# Revit family: 18-P-SD
name_source: partatom
category: Lighting Fixtures
revit_build: Autodesk Revit 2014 (Build: 20130308_1515(x64)
units: mm (PartAtom-declared; Revit-internal decimal feet)

## types (3) — shared parameters
Apparent Load = 0 VA
Assembly Code = D5020200
Circuiting = 1C 1 Circuit,2C 2 Circuit-In Board/ Out Board,AC Alternate Lamp Compart Switch
Color Filter = 16777215
Default Elevation = 4' - 0"
Description = The SDx is a semi-direct extruded aluminum fixture which can be pendant- or surface-mounted, using T8, T5, or T5HO lamps.
Diffuser = Blade Baffle, White/ Acrylic Blade Baffle, Green/ Parabolic Baffle, Semi-Specular Aluminum
Dimming Lamp Color Temperature Shift = <None>
Emit Shape Visible in Rendering = No
Emit from Rectangle Length = 0' - 4 1/2"
Finish/ Color = C1 CWM- Matte White,C2 TCWM- Textured Matte White,C3 CSL- Light Silver,C4 CMA- Machined Aluminum,C5 CCB- Carbon Black,C6 TCBC- Textured Camera Black,CC CXY- Custom Color
Fixture Distribution = Semi-Direct
Glass = Glass - Hubbell - White
Housing Material = Paint - Hubbell - Matte White
Lamp = 1T5 1-Light T5 Lamping,2T5 2-Light T5 Lamping,1T5HO 1-Light T5HO Lamping,2T5HO 2-Light T5HO Lamping,1T8 1-Light T8 Lamping,2T8 2-Light T8 Lamping
Load Classification = Lighting
Manufacturer = Litecontrol Lighting
Model = SDx Pendant Semi-Direct
Mounting = Pendant
Photometric Link = https://www.hubbell.com
Photometric Notes = More IES files download on Photometric Link
Photometric Web File = 18-P-SD-04-BW-Cx-1T5HO.ies
Power Factor = 1
Product Documentation Link = https://hubbellcdn.com
Product Page URL = https://www.hubbell.com
Tilt Angle = -90.00°
Type Comments = Lighting Fixture
URL = https://www.hubbell.com
Voltage = 120 V
Warranty = 5-Years Warranty

## per-type parameters (varying)
| type | Emit from Rectangle Width | zz Length 1 |
| 18-P-SD-04' | 3' - 11" | 4' - 0" |
| 18-P-SD-08' | 7' - 11" | 8' - 0" |
| 18-P-SD-12' | 11' - 11" | 12' - 0" |

## geometry (parser evidence)
native form markers: Sweep x5
no freeform markers — native parametric forms only
